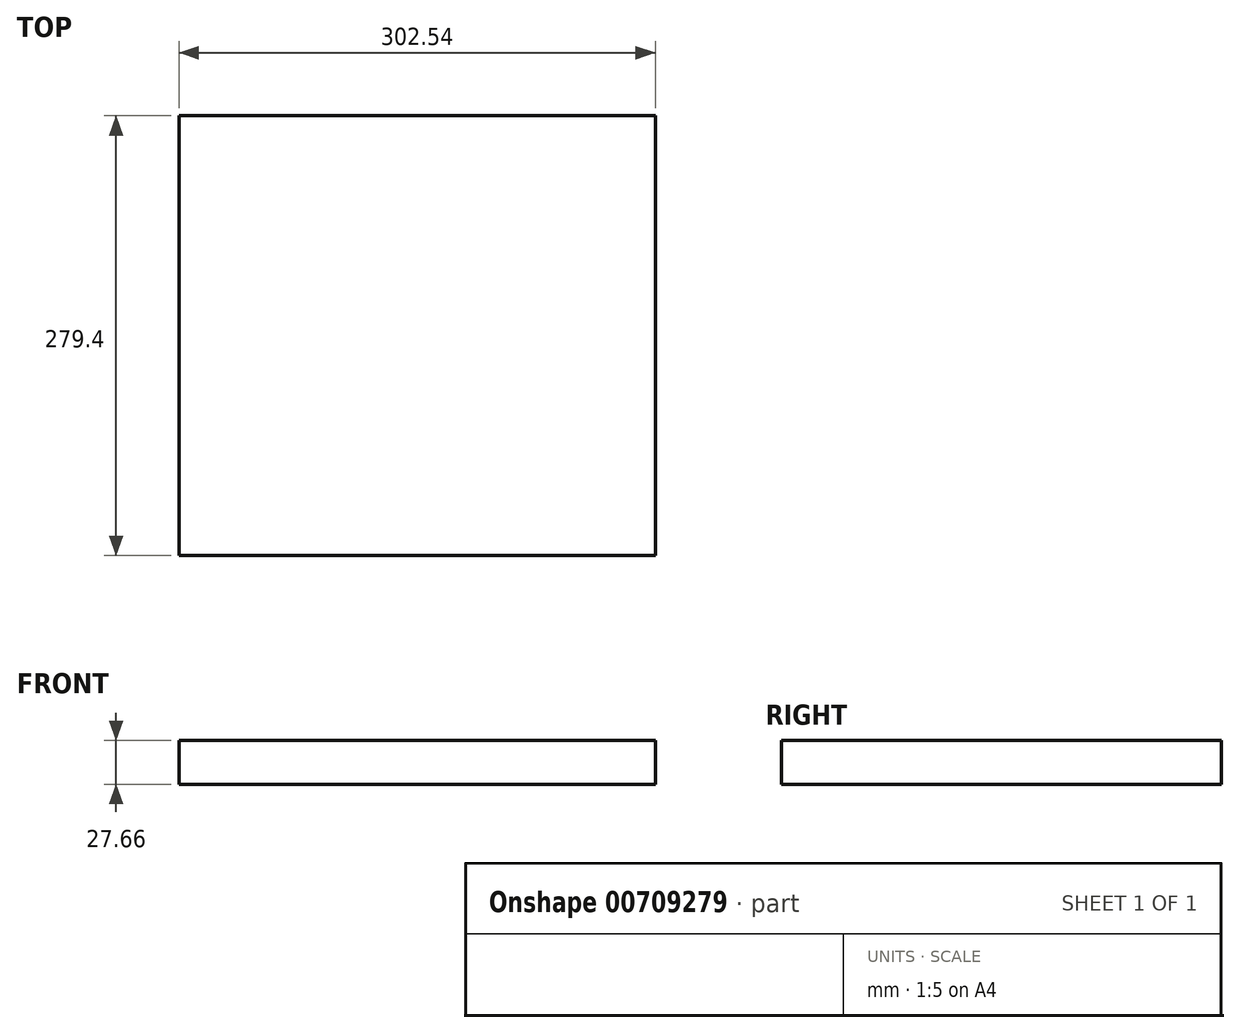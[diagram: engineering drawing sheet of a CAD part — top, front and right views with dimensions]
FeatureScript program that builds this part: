
annotation { "Feature Type Name" : "Feature", "Feature Type Description" : "" }
export const myFeature = defineFeature(function(context is Context, id is Id, definition is map)
    precondition{}
    {
        {
            var Q0;
            Q0=qCreatedBy(makeId("Front.planeOp"),FACE);
            var sketch = newSketch(context, id + "F0", { "sketchPlane" : qUnion([Q0])});
            skLineSegment(sketch, "E0.bottom", {"start": v(-151.27, -13.83) * mm, "end": v(151.27, -13.83) * mm});
            skLineSegment(sketch, "E0.top", {"start": v(-151.27, 13.83) * mm, "end": v(151.27, 13.83) * mm});
            skLineSegment(sketch, "E0.left", {"start": v(-151.27, -13.83) * mm, "end": v(-151.27, 13.83) * mm});
            skLineSegment(sketch, "E0.right", {"start": v(151.27, -13.83) * mm, "end": v(151.27, 13.83) * mm});
            skPoint(sketch, "E0.middle", {"position": v(0, 0) * mm});
            skSolve(sketch);
        }
        {
            var Q0;
            Q0 = qSketchRegion(id + "F0", true);
            extrude(context, id + "F1", {"entities" : qUnion([Q0]), "depth" : 279.4 * mm, "offsetDistance" : 25.4 * mm});
        }
    });
